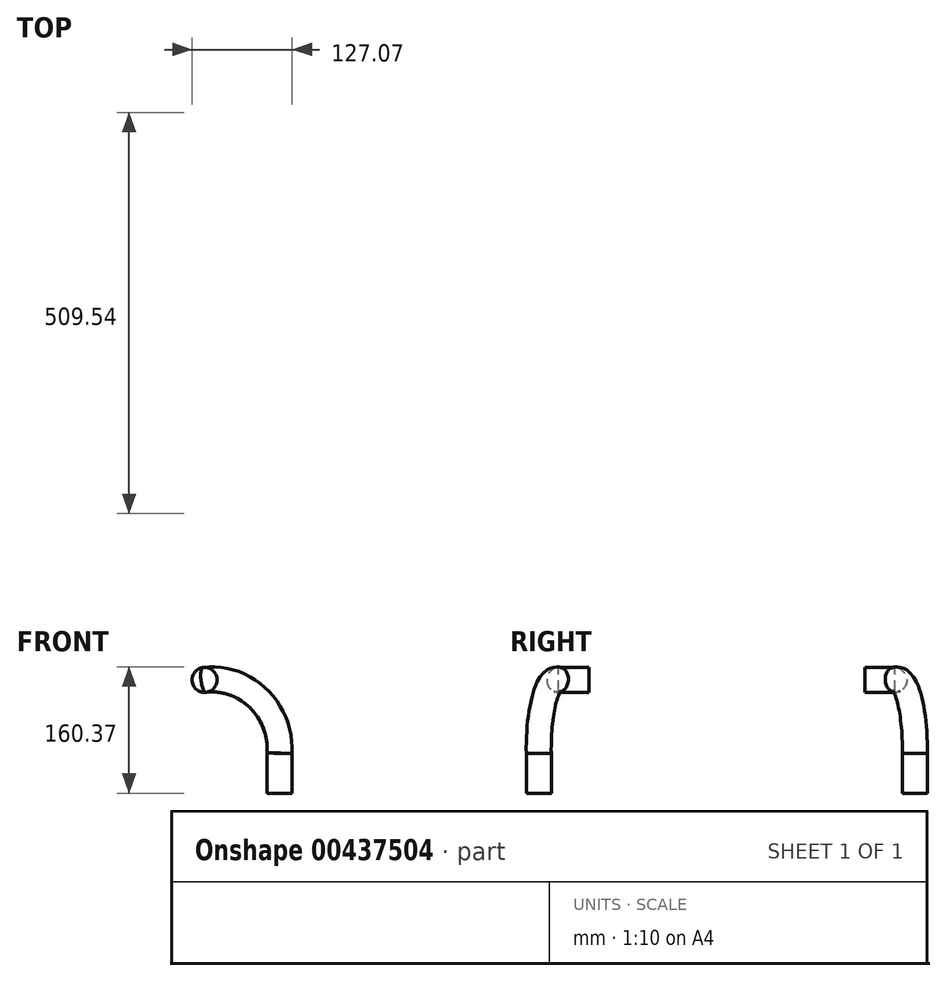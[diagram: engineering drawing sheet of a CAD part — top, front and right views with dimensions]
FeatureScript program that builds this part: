
annotation { "Feature Type Name" : "Feature", "Feature Type Description" : "" }
export const myFeature = defineFeature(function(context is Context, id is Id, definition is map)
    precondition{}
    {
        {
            var Q0;
            Q0=qCreatedBy(makeId("Front.planeOp"),FACE);
            var sketch = newSketch(context, id + "F0", { "sketchPlane" : qUnion([Q0])});
            skCircle(sketch, "E0", {"center": v(0, 0) * mm, "radius": 15.88 * mm});
            skSolve(sketch);
        }
        {
            var Q0;
            Q0=qCreatedBy(makeId("Right.planeOp"),FACE);
            var sketch = newSketch(context, id + "F1", { "sketchPlane" : qUnion([Q0])});
            skLineSegment(sketch, "E1", {"start": v(0, 0) * mm, "end": v(-38.1, 0) * mm});
            skSolve(sketch);
        }
        {
            var Q0;
            Q0=qCreatedBy(makeId("Front.planeOp"),FACE);
            cPlane(context, id + "F2", {"entities" : qUnion([Q0]), "cplaneType" : CPlaneType.OFFSET, "offset" : 50.8 * mm, "width" : 152.4 * mm, "height" : 152.4 * mm});
        }
        {
            var Q0;
            Q0=qCreatedBy(makeId("Top.planeOp"),FACE);
            var sketch = newSketch(context, id + "F3", { "sketchPlane" : qUnion([Q0])});
            skLineSegment(sketch, "E2", {"start": v(0, -38.1) * mm, "end": v(75.72, -58.39) * mm});
            skLineSegment(sketch, "E3", {"start": v(0, 0) * mm, "end": v(0, -38.1) * mm});
            skLineSegment(sketch, "E4", {"start": v(0, -38.1) * mm, "end": v(45.03, -38.1) * mm});
            skSolve(sketch);
        }
        {
            var Q0;
            Q0=qCreatedBy(id+"F2.planeOp",FACE);
            var Q1;
            Q1=sQuery(id+"F3.wireOp",EDGE,"E2");
            cPlane(context, id + "F4", {"entities" : qUnion([Q0, Q1]), "cplaneType" : CPlaneType.LINE_ANGLE, "offset" : 25.4 * mm, "angle" : 0 * degree, "width" : 152.4 * mm, "height" : 152.4 * mm});
        }
        {
            var Q0;
            Q0=qCreatedBy(id+"F4.planeOp",FACE);
            var sketch = newSketch(context, id + "F5", { "sketchPlane" : qUnion([Q0])});
            skArc(sketch, "E5", {"start": v(-9.86, 0) * mm, "mid": v(-80.8, -23.63) * mm, "end": v(-108.39, -93.12) * mm});
            skLineSegment(sketch, "E6", {"start": v(-108.39, -93.12) * mm, "end": v(-108.39, -143.92) * mm});
            skSolve(sketch);
        }
        {
            var Q0;
            Q0=makeQuery(id+"F0.imprint","IMPRINT",FACE,{"disambiguationData":[TD([[makeQuery(id+"F0.imprint","IMPRINT",EDGE,{"derivedFrom":sQuery(id+"F0.wireOp",EDGE,"E0")}),1.0]])]});
            var Q1;
            Q1=sQuery(id+"F1.wireOp",EDGE,"E1");
            var Q2;
            Q2=sQuery(id+"F5.wireOp",EDGE,"E5");
            var Q3;
            Q3=sQuery(id+"F5.wireOp",EDGE,"E6");
            sweep(context, id + "F6", {"profiles" : qUnion([Q0]), "path" : qUnion([Q1, Q2, Q3])});
        }
        {
            var Q0;
            Q0=makeQuery(id+"F6.opSweep","MID_CAP_EDGE",EDGE,{"disambiguationData":[OSD([sQuery(id+"F0.wireOp",EDGE,"E0"),sQuery(id+"F5.wireOp",VERTEX,"E5.start")]),OD(0.0)],"capPos":1.0});
            fillet(context, id + "F7", {"entities" : qUnion([Q0]), "radius" : 15.24 * mm, "tangentPropagation" : true, "allowEdgeOverflow" : false});
        }
        {
            var Q0;
            Q0=qCreatedBy(makeId("Front.planeOp"),FACE);
            cPlane(context, id + "F8", {"entities" : qUnion([Q0]), "cplaneType" : CPlaneType.OFFSET, "offset" : 175.26 * mm, "oppositeDirection" : true, "width" : 152.4 * mm, "height" : 152.4 * mm});
        }
        {
            var Q0;
            Q0=makeQuery(id+"F6.opSweep","SWEPT_BODY",BODY,{"disambiguationData":[OSD([sQuery(id+"F0.wireOp",EDGE,"E0"),sQuery(id+"F5.wireOp",EDGE,"E6")])]});
            var Q1;
            Q1=qCreatedBy(id+"F8.planeOp",FACE);
            mirror(context, id + "F9", {"operationType" : NewBodyOperationType.ADD, "entities" : qUnion([Q0]), "mirrorPlane" : qUnion([Q1])});
        }
    });
